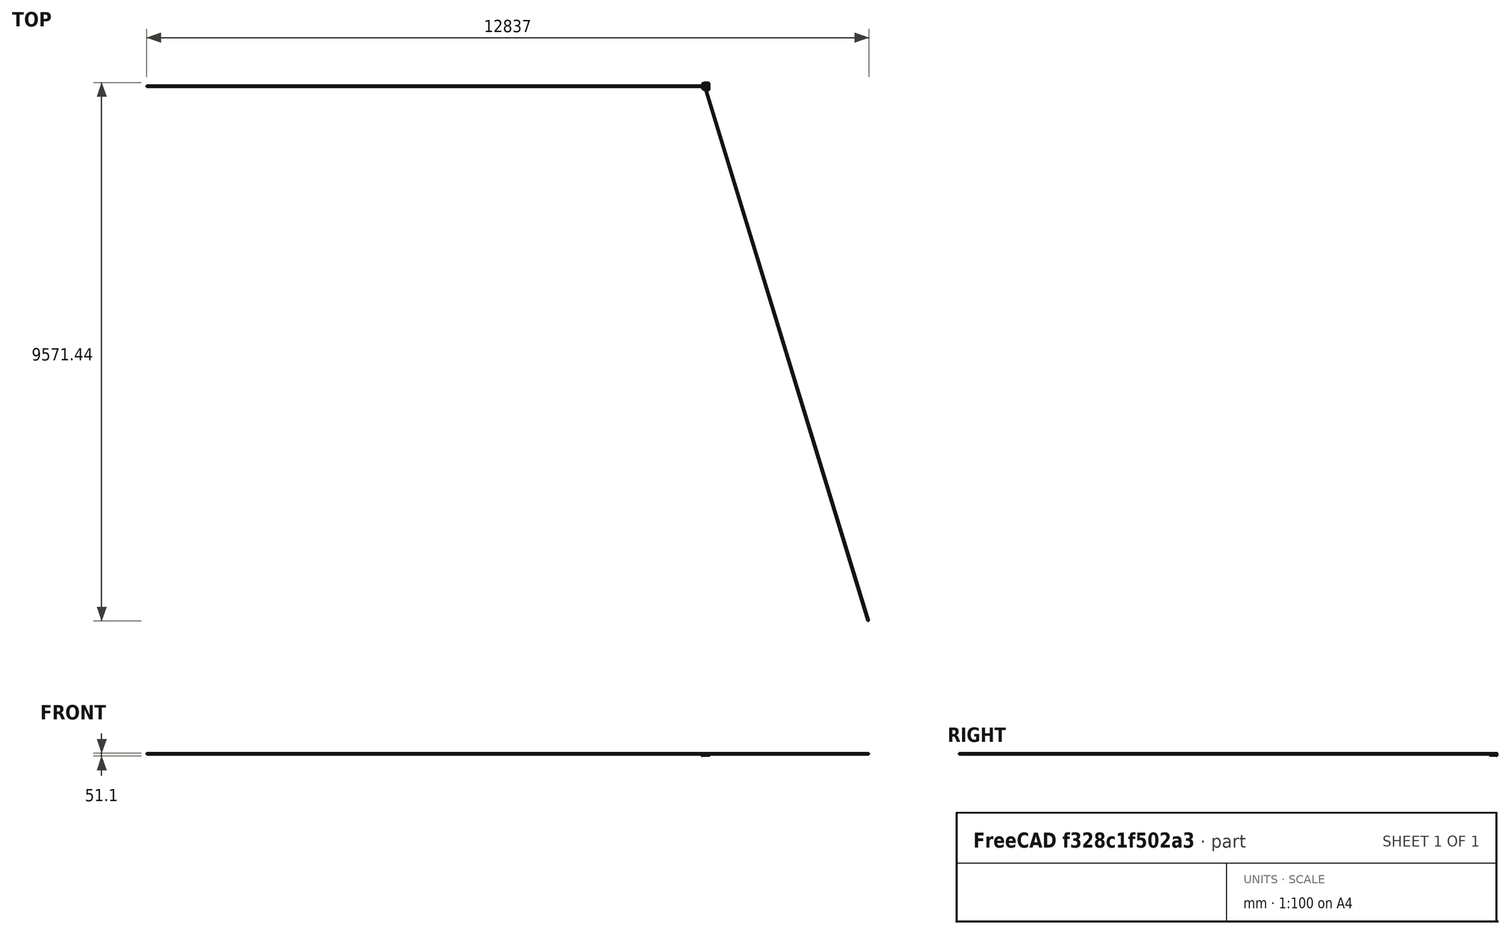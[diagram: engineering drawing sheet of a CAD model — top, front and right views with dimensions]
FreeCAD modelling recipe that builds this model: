
FCSTD DOCUMENT  (FreeCAD 0.16R)
Label: chainguard25TRearRev5
License: All rights reserved
LicenseURL: http://en.wikipedia.org/wiki/All_rights_reserved
objects: Sketcher::SketchObject×12, PartDesign::Pocket×6, PartDesign::Pad×5, PartDesign::Fillet×5, Part::FeaturePython×4, Mesh::Feature×4
note: 43 computed .brp shape members not serialized (recipe doc carries the construction recipe); baked Part::Feature solids carry a one-line shape summary decoded from their .brp

FEATURE [Sketcher::SketchObject] Sketch001
  sketch-geometry (7):
    g0: LineSegment StartX=60 StartY=64 StartZ=0 EndX=0 EndY=64 EndZ=0
    g1: LineSegment StartX=60 StartY=-64 StartZ=0 EndX=0 EndY=-64 EndZ=0
    g2: ArcOfCircle CenterX=8.21903e-05 CenterY=0 CenterZ=0 NormalX=0 NormalY=0 NormalZ=1 Radius=64 StartAngle=1.5708 EndAngle=4.71239
    g3: Circle CenterX=0 CenterY=0 CenterZ=0 NormalX=0 NormalY=0 NormalZ=1 Radius=45
    g4: ArcOfCircle CenterX=60 CenterY=51 CenterZ=0 NormalX=0 NormalY=0 NormalZ=1 Radius=13 StartAngle=0 EndAngle=1.5708
    g5: ArcOfCircle CenterX=60 CenterY=-51 CenterZ=0 NormalX=0 NormalY=0 NormalZ=1 Radius=13 StartAngle=4.71239 EndAngle=6.28319
    g6: LineSegment StartX=73 StartY=51 StartZ=0 EndX=73 EndY=-51 EndZ=0
  constraints (23):
    c: Horizontal(g0)
    c: Horizontal(g1)
    c: Coincident(g2,g1)
    c: Coincident(g0,g2)
    c: DistanceX(g1,g0) = 0
    c: Equal(g0,g1)
    c: DistanceY(g1,g0) = 128
    c: Radius(g2) = 64
    c: Symmetric(g1,g0,g-1)
    c: Radius(g3) = 45
    c: Coincident(g3,g-1)
    c: PointOnObject(g4,g0)
    c: Radius(g4) = 13
    c: DistanceX(g0,g0) = 60
    c: Equal(g5,g4)
    c: Vertical(g6)
    c: DistanceX(g-1,g6) = 73
    c: Symmetric(g6,g6,g-1)
    c: DistanceY(g6,g6) = 102
    c: Coincident(g4,g6)
    c: Coincident(g5,g6)
    c: Coincident(g1,g5)
    c: Coincident(g0,g4)
FEATURE [PartDesign::Pad] Pad  label="Faceplate"
  Length = 1.12
  Length2 = 100
  Reversed = true
  Sketch = -> Sketch001
  Type = 0
FEATURE [Sketcher::SketchObject] Sketch002
  sketch-geometry (8):
    g0: LineSegment StartX=60 StartY=64 StartZ=0 EndX=0 EndY=64 EndZ=0
    g1: LineSegment StartX=60 StartY=-64 StartZ=0 EndX=0 EndY=-64 EndZ=0
    g2: ArcOfCircle CenterX=6.44712e-05 CenterY=0 CenterZ=0 NormalX=0 NormalY=0 NormalZ=1 Radius=64 StartAngle=1.5708 EndAngle=4.71239
    g3: LineSegment StartX=0 StartY=62 StartZ=0 EndX=60 EndY=62 EndZ=0
    g4: LineSegment StartX=0 StartY=-62 StartZ=0 EndX=60 EndY=-62 EndZ=0
    g5: LineSegment StartX=60 StartY=64 StartZ=0 EndX=60 EndY=62 EndZ=0
    g6: LineSegment StartX=60 StartY=-62 StartZ=0 EndX=60 EndY=-64 EndZ=0
    g7: ArcOfCircle CenterX=1.45954e-05 CenterY=0 CenterZ=0 NormalX=0 NormalY=0 NormalZ=1 Radius=62 StartAngle=1.5708 EndAngle=4.71239
  constraints (25):
    c: Horizontal(g0)
    c: Horizontal(g1)
    c: Coincident(g2,g1)
    c: Coincident(g0,g2)
    c: DistanceX(g1,g0) = 0
    c: Equal(g0,g1)
    c: DistanceY(g1,g0) = 128
    c: Radius(g2) = 64
    c: Symmetric(g1,g0,g-1)
    c: Radius(g7) = 62
    c: Parallel(g0,g3)
    c: DistanceY(g3,g0) = 2
    c: DistanceY(g1,g4) = 2
    c: Parallel(g4,g1)
    c: DistanceX(g0,g3) = 0
    c: DistanceX(g4) = 0
    c: DistanceX(g0) = 60
    c: Equal(g3,g0)
    c: Equal(g4,g0)
    c: Coincident(g4,g6)
    c: Coincident(g6,g1)
    c: Coincident(g5,g3)
    c: Coincident(g5,g0)
    c: Coincident(g7,g3)
    c: Coincident(g7,g4)
FEATURE [PartDesign::Pad] Pad001  label="Connector"
  Length = 12
  Length2 = 100
  Sketch = -> Sketch002
  Type = 0
FEATURE [Sketcher::SketchObject] Sketch017
  sketch-geometry (5):
    g0: LineSegment [constr] StartX=-6 StartY=2 StartZ=0 EndX=-29.8283 EndY=79.9388 EndZ=0
    g1: LineSegment StartX=-7.74339 StartY=67.5577 StartZ=0 EndX=-41.2141 EndY=57.3247 EndZ=0
    g2: LineSegment StartX=-41.2141 StartY=57.3247 StartZ=0 EndX=-39.4598 EndY=51.5868 EndZ=0
    g3: LineSegment StartX=-39.4598 StartY=51.5868 StartZ=0 EndX=-5.98916 EndY=61.8199 EndZ=0
    g4: LineSegment StartX=-5.98916 StartY=61.8199 StartZ=0 EndX=-7.74339 EndY=67.5577 EndZ=0
  constraints (15):
    c: DistanceY(g-1,g0) = 2
    c: DistanceX(g-1,g0) = -6
    c: Angle(g0) = 1.8675
    c: Coincident(g1,g2)
    c: Coincident(g2,g3)
    c: Coincident(g3,g4)
    c: Coincident(g1,g4)
    c: Parallel(g2,g4)
    c: Parallel(g1,g3)
    c: Perpendicular(g2,g1)
    c: Distance(g4) = 6
    c: Distance(g1) = 35
    c: Symmetric(g3,g2,g0)
    c: Distance(g-1,g1) = 68
    c: Distance(g0) = 81.5
FEATURE [Sketcher::SketchObject] Sketch020
  sketch-geometry (4):
    g0: LineSegment StartX=67 StartY=35 StartZ=0 EndX=73 EndY=35 EndZ=0
    g1: LineSegment StartX=73 StartY=35 StartZ=0 EndX=73 EndY=-25 EndZ=0
    g2: LineSegment StartX=73 StartY=-25 StartZ=0 EndX=67 EndY=-25 EndZ=0
    g3: LineSegment StartX=67 StartY=-25 StartZ=0 EndX=67 EndY=35 EndZ=0
  constraints (12):
    c: Coincident(g0,g1)
    c: Coincident(g1,g2)
    c: Coincident(g2,g3)
    c: Coincident(g3,g0)
    c: Horizontal(g0)
    c: Horizontal(g2)
    c: Vertical(g1)
    c: Vertical(g3)
    c: DistanceX(g-1,g0) = 73
    c: DistanceX(g0,g0) = 6
    c: DistanceY(g-1,g0) = 35
    c: DistanceY(g1,g1) = 60
FEATURE [PartDesign::Pad] Pad004  label="SyncBoss"
  Length = 31
  Length2 = 100
  Sketch = -> Sketch020
  Type = 0
FEATURE [Sketcher::SketchObject] Sketch021
  ExternalGeometry = -> [Pad004]
  Placement = pos=(73,0,0) rot=(0.57735,0.57735,0.57735;2.0944rad)
  Support = -> Pad004 [Face2]
  sketch-geometry (1):
    g0: Circle CenterX=5 CenterY=31 CenterZ=0 NormalX=0 NormalY=0 NormalZ=1 Radius=11.2
  constraints (2):
    c: Symmetric(g-4,g-3,g0)
    c: Radius(g0) = 11.2
FEATURE [PartDesign::Pocket] Pocket  label="SyncHole"
  Length = 5
  Sketch = -> Sketch021
  Type = 1
FEATURE [PartDesign::Pad] Pad005  label="STBoss"
  Length = 32
  Length2 = 1
  Sketch = -> Sketch017
  Type = 4
FEATURE [Sketcher::SketchObject] Sketch022
  ExternalGeometry = -> [Pad005]
  Placement = pos=(-19.5508,63.9478,0) rot=(-0.105093,0.703191,0.703191;3.35101rad)
  Support = -> Pad005 [Face1]
  sketch-geometry (1):
    g0: Circle CenterX=5.15309 CenterY=32 CenterZ=0 NormalX=0 NormalY=0 NormalZ=1 Radius=11.2
  constraints (2):
    c: Symmetric(g-4,g-3,g0)
    c: Radius(g0) = 11.2
FEATURE [PartDesign::Pocket] Pocket006  label="SThole"
  Length = 5
  Sketch = -> Sketch022
  Type = 1
FEATURE [Sketcher::SketchObject] Sketch023
  Placement = pos=(-19.5508,63.9478,0) rot=(-0.105093,0.703191,0.703191;3.35101rad)
  Support = -> Pocket006 [Face1]
  sketch-geometry (3):
    g0: LineSegment StartX=31.754 StartY=21.6568 StartZ=0 EndX=10.7035 EndY=-1 EndZ=0
    g1: LineSegment StartX=10.7035 StartY=-1 StartZ=0 EndX=40.8501 EndY=-7.90189 EndZ=0
    g2: LineSegment StartX=40.8501 StartY=-7.90189 StartZ=0 EndX=31.754 EndY=21.6568 EndZ=0
  constraints (9):
    c: Coincident(g0,g1)
    c: Coincident(g1,g2)
    c: Coincident(g0,g2)
    c: Equal(g0,g2)
    c: Equal(g2,g1)
    c: DistanceY(g0,g-1) = 1
    c: Angle(g1) = -0.225065
    c: Distance(g2) = 30.9266
    c: DistanceX(g-1,g0) = 10.7035
FEATURE [PartDesign::Pocket] Pocket007  label="STbevel1"
  Length = 6
  Sketch = -> Sketch023
  Type = 0
FEATURE [Sketcher::SketchObject] Sketch024
  sketch-geometry (6):
    g0: ArcOfCircle CenterX=0 CenterY=0 CenterZ=0 NormalX=0 NormalY=0 NormalZ=1 Radius=48 StartAngle=1.34179 EndAngle=4.9414
    g1: Circle CenterX=0 CenterY=0 CenterZ=0 NormalX=0 NormalY=0 NormalZ=1 Radius=45
    g2: LineSegment StartX=10.8966 StartY=46.7468 StartZ=0 EndX=65 EndY=35.4994 EndZ=0
    g3: LineSegment StartX=65 StartY=35.5006 StartZ=0 EndX=65 EndY=-35.4994 EndZ=0
    g4: LineSegment StartX=65 StartY=-35.4994 StartZ=0 EndX=10.8966 EndY=-46.7468 EndZ=0
    g5: LineSegment StartX=65 StartY=35.5 StartZ=0 EndX=65 EndY=-35.5 EndZ=0
  constraints (14):
    c: Coincident(g0,g-1)
    c: Radius(g0) = 48
    c: Coincident(g1,g-1)
    c: Radius(g1) = 45
    c: Coincident(g3,g4)
    c: Coincident(g0,g2)
    c: Distance(g3) = 71
    c: DistanceX(g-1,g2) = 65
    c: Equal(g4,g2)
    c: Vertical(g3)
    c: Symmetric(g2,g3,g-1)
    c: Distance(g2) = 55.2601
    c: DistanceY(g-1,g0) = 46.7468
    c: DistanceX(g0) = 10.8966
FEATURE [Sketcher::SketchObject] Sketch026
  sketch-geometry (4):
    g0: LineSegment StartX=0 StartY=47.5 StartZ=0 EndX=73 EndY=35 EndZ=0
    g1: LineSegment StartX=73 StartY=35 StartZ=0 EndX=73 EndY=-35 EndZ=0
    g2: LineSegment StartX=73 StartY=-35 StartZ=0 EndX=0 EndY=-47.5 EndZ=0
    g3: LineSegment StartX=0 StartY=-47.5 StartZ=0 EndX=0 EndY=47.5 EndZ=0
  constraints (11):
    c: Coincident(g0,g1)
    c: Coincident(g1,g2)
    c: Coincident(g2,g3)
    c: Coincident(g3,g0)
    c: Symmetric(g2,g0,g-1)
    c: Symmetric(g2,g0,g-1)
    c: Equal(g0,g2)
    c: Vertical(g1)
    c: DistanceY(g1,g1) = 70
    c: DistanceY(g3,g3) = 95
    c: DistanceX(g-1,g0) = 73
FEATURE [PartDesign::Pad] Pad007  label="FieldStiffener"
  Length = 1
  Length2 = 100
  Sketch = -> Sketch026
  Type = 0
FEATURE [Sketcher::SketchObject] Sketch028
  ExternalGeometry = -> [Pocket]
  Placement = pos=(0,0,31) rot=(0,0,1;0rad)
  Support = -> Pocket [Face5]
  sketch-geometry (2):
    g0: Circle CenterX=70 CenterY=19 CenterZ=0 NormalX=0 NormalY=0 NormalZ=1 Radius=1.4
    g1: Circle CenterX=70 CenterY=-9 CenterZ=0 NormalX=0 NormalY=0 NormalZ=1 Radius=1.4
  constraints (6):
    c: DistanceY(g-4,g0) = 2.8
    c: DistanceX(g0,g-4) = 3
    c: DistanceX(g1,g-6) = 3
    c: DistanceY(g1,g-5) = 2.8
    c: Equal(g1,g0)
    c: Radius(g1) = 1.4
FEATURE [PartDesign::Pocket] Pocket010  label="SyncScrewHoles"
  Length = 15
  Sketch = -> Sketch028
  Type = 0
FEATURE [Sketcher::SketchObject] Sketch029
  ExternalGeometry = -> [Pocket010]
  Placement = pos=(73,0,0) rot=(0.57735,0.57735,0.57735;2.0944rad)
  Support = -> Pocket010 [Face3]
  sketch-geometry (6):
    g0: LineSegment StartX=35 StartY=3 StartZ=0 EndX=22.5 EndY=32 EndZ=0
    g1: LineSegment StartX=22.5 StartY=32 StartZ=0 EndX=-12.5 EndY=32 EndZ=0
    g2: LineSegment StartX=-12.5 StartY=32 StartZ=0 EndX=-25 EndY=3 EndZ=0
    g3: LineSegment StartX=-25 StartY=3 StartZ=0 EndX=-28.2949 EndY=52.1665 EndZ=0
    g4: LineSegment StartX=-28.2949 StartY=52.1665 StartZ=0 EndX=43.0613 EndY=52.1665 EndZ=0
    g5: LineSegment StartX=43.0613 StartY=52.1665 StartZ=0 EndX=35 EndY=3 EndZ=0
  constraints (18):
    c: Coincident(g0,g1)
    c: Horizontal(g1)
    c: Coincident(g1,g2)
    c: Coincident(g2,g3)
    c: Coincident(g3,g4)
    c: Horizontal(g4)
    c: Coincident(g4,g5)
    c: Coincident(g0,g5)
    c: DistanceX(g-4,g0) = 6.3
    c: DistanceX(g1,g-4) = 6.3
    c: DistanceX(g-3,g0) = 0
    c: DistanceX(g2,g-6) = 0
    c: DistanceX(g4,g4) = 71.3562
    c: Distance(g3) = 49.2768
    c: Distance(g5) = 49.823
    c: DistanceY(g-4,g1) = 1
    c: DistanceY(g-6,g2) = 3
    c: DistanceY(g-3,g0) = 3
FEATURE [PartDesign::Pocket] Pocket011  label="SyncBigBevel"
  Length = 5
  Sketch = -> Sketch029
  Type = 1
FEATURE [PartDesign::Fillet] Fillet  label="SyncFillets"
  Base = -> Pocket011 [Edge13,Edge14,Edge15,Edge3,Edge9,Edge21,Edge19,Edge22]
  Radius = 1
FEATURE [Sketcher::SketchObject] Sketch030
  ExternalGeometry = -> [Pocket007]
  Placement = pos=(0,0,32) rot=(0,0,1;0rad)
  Support = -> Pocket007 [Face5]
  sketch-geometry (2):
    g0: Circle CenterX=-37.0422 CenterY=55.5316 CenterZ=0 NormalX=0 NormalY=0 NormalZ=1 Radius=1.4
    g1: Circle CenterX=-10.2466 CenterY=63.6553 CenterZ=0 NormalX=0 NormalY=0 NormalZ=1 Radius=1.4
  constraints (6):
    c: Equal(g0,g1)
    c: Radius(g0) = 1.4
    c: Distance(g1,g-6) = 3
    c: Distance(g0,g1) = 28
    c: Distance(g0,g-8) = 4.08
    c: Distance(g1,g-6) = 4.08
FEATURE [PartDesign::Pocket] Pocket012
  Length = 15
  Sketch = -> Sketch030
  Type = 0
FEATURE [PartDesign::Fillet] Fillet001  label="STfillets"
  Base = -> Pocket012 [Edge23,Edge7,Edge8,Edge20,Edge12,Edge13,Edge14,Edge3,Edge2,Edge10,Edge11,Edge9,Edge1]
  Radius = 2
FEATURE [PartDesign::Fillet] Fillet002
  Base = -> Pad001 [Edge24,Edge13]
  Radius = 10
FEATURE [PartDesign::Fillet] Fillet003
  Base = -> Pad [Edge4,Edge7,Edge10,Edge13,Edge16,Edge18,Edge21]
  Radius = 0.6
FEATURE [PartDesign::Fillet] Fillet004
  Base = -> Fillet002 [Edge17]
  Radius = 1
FEATURE [Part::FeaturePython] refine  label="refine_Fillet004"  # WARN: FeaturePython — macro-defined, semantics opaque (R4)
  Base = -> Fillet004
FEATURE [Part::FeaturePython] refine001  label="refine_Fillet003"  # WARN: FeaturePython — macro-defined, semantics opaque (R4)
  Base = -> Fillet003
FEATURE [Part::FeaturePython] refine002  label="refine_STfillets"  # WARN: FeaturePython — macro-defined, semantics opaque (R4)
  Base = -> Fillet001
FEATURE [Part::FeaturePython] refine003  label="refine_SyncFillets"  # WARN: FeaturePython — macro-defined, semantics opaque (R4)
  Base = -> Fillet
FEATURE [Mesh::Feature] Mesh  label="refine_Fillet004 (Meshed)"
FEATURE [Mesh::Feature] Mesh001  label="refine_Fillet003 (Meshed)"
FEATURE [Mesh::Feature] Mesh002  label="refine_STfillets (Meshed)"
FEATURE [Mesh::Feature] Mesh003  label="refine_SyncFillets (Meshed)"
